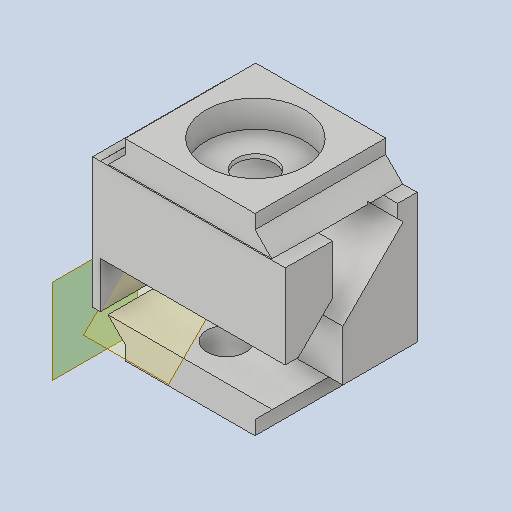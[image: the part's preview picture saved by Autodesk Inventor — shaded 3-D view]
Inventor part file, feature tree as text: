
AUTODESK INVENTOR PART (.ipt)
format: ipt  version: 2022 (Build 260153000, 153)  size: 288,256 bytes
history: native  units: mm
features: extrude x10, sketch x10, plane x6, projected_geometry x6, other x3, reference x1
ambient origin geometry x8: Origin, YZ Plane, XZ Plane, XY Plane, X Axis, Y Axis, Z Axis, Center Point
bodies: Solid1 (feature_tree)
feature tree (36):
  extrude  "Extrusion1"  Depth=24.9mm
  plane  "Work Plane2"
  sketch  "Sketch13"  dims[d20=3.14mm d21=26.9mm]
  plane  "Work Plane3"
  extrude  "Extrusion12"  Depth=26.9mm
  extrude  "Extrusion13"  Depth=3.0mm TaperAngle=0.0deg
  extrude  "Extrusion16"  Depth=25.5mm
  plane  "Work Plane4"
  plane  "Work Plane6"
  extrude  "Extrusion20"  Depth=7.0mm
  plane  "Work Plane8"
  plane  "Work Plane5"
  extrude  "Extrusion27"  Depth=10.0mm TaperAngle=0.0deg
  extrude  "Extrusion28"  TaperAngle=0.0deg  [1 undecoded]
  extrude  "Extrusion29"  Depth=10.0mm TaperAngle=0.0deg
  extrude  "Extrusion30"  Depth=10.0mm TaperAngle=0.0deg
  extrude  "Extrusion31"  Depth=2.0mm
  sketch  "Sketch1"  dims[d17=45.0deg d18=24.9mm]
  projected_geometry  "Projected Loop7"
  sketch  "Sketch14"  dims[d22=15.0mm d23=3.0mm d24=0.0mm]
  reference  "Reference12"
  sketch  "Sketch17"  dims[d59=1.0mm d60=0.0mm d61=25.5mm]
  sketch  "Sketch21"  dims[d62=7.0mm d63=0.0mm d72=33.5mm]
  projected_geometry  "Projected Loop15"
  sketch  "Skizze29"  dims[d73=0.0mm d74=0.0mm d95=10.0mm d96=0.0mm]
  sketch  "Skizze30"  dims[d105=5.0mm d133=0.0mm d134=0.0mm]
  sketch  "Skizze31"  dims[d135=10.0mm d136=10.0mm d137=0.0mm]
  sketch  "Skizze32"  dims[d138=10.0mm d139=10.0mm d140=0.0mm]
  projected_geometry  "Projizierte Kontur25"
  projected_geometry  "Projizierte Kontur26"
  sketch  "Skizze33"  dims[d141=2.0mm d142=0.0mm d143=1.0mm d144=2.0mm d145=0.0mm]
  projected_geometry  "Projizierte Kontur27"
  projected_geometry  "Projizierte Kontur28"
  other  "Assembly_Cube_Dichroic_Beamsplitter.iam"
  other  "Assembly_Cube_empty_1x1_v2:1"
  other  "10_Cube_1x1_v2:1"
note: 1 required parameter value undecoded (feature->parameter linkage not recoverable at this tier; creation-order binding heuristic only, values carry confidence <= 0.55)
